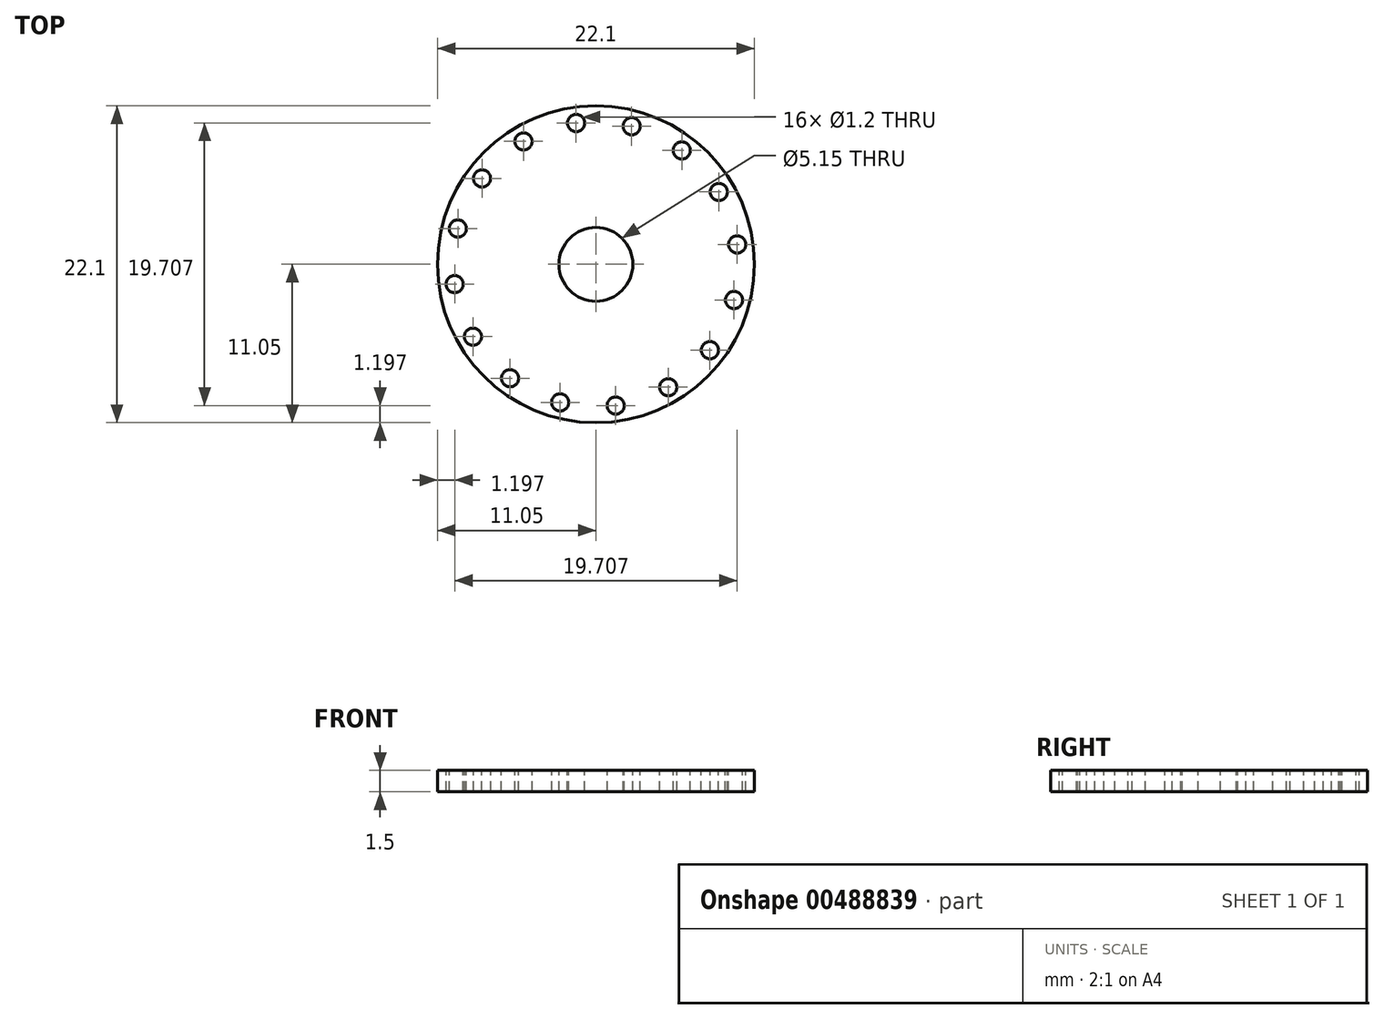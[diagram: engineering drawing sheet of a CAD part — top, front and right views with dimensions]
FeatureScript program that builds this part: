
annotation { "Feature Type Name" : "Feature", "Feature Type Description" : "" }
export const myFeature = defineFeature(function(context is Context, id is Id, definition is map)
    precondition{}
    {
        {
            var Q0;
            Q0=qCreatedBy(makeId("Top.planeOp"),FACE);
            var sketch = newSketch(context, id + "F0", { "sketchPlane" : qUnion([Q0])});
            skCircle(sketch, "E0", {"center": v(0, 0) * mm, "radius": 11.05 * mm});
            skSolve(sketch);
        }
        {
            var Q0;
            Q0=makeQuery(id+"F0.imprint","IMPRINT",FACE,{"disambiguationData":[TD([[makeQuery(id+"F0.imprint","IMPRINT",EDGE,{"derivedFrom":sQuery(id+"F0.wireOp",EDGE,"E0")}),1.0]])]});
            extrude(context, id + "F1", {"entities" : qUnion([Q0]), "depth" : 1.5 * mm, "offsetDistance" : 25 * mm});
        }
        {
            var Q0;
            Q0=makeQuery(id+"F1.opExtrude","CAP_FACE",FACE,{"disambiguationData":[OSD([sQuery(id+"F0.wireOp",EDGE,"E0")])],"isStart":false});
            var sketch = newSketch(context, id + "F2", { "sketchPlane" : qUnion([Q0])});
            skCircle(sketch, "E1", {"center": v(5.99, 7.95) * mm, "radius": 0.6 * mm});
            skPoint(sketch, "E2.center", {"position": v(0, 0) * mm});
            skCircle(sketch, "E3", {"center": v(0, 0) * mm, "radius": 2.58 * mm});
            skLineSegment(sketch, "E4", {"start": v(-5.78, -7.67) * mm, "end": v(0, 0) * mm, "construction": true});
            skCircle(sketch, "E5.1.0", {"center": v(2.5, 9.63) * mm, "radius": 0.6 * mm});
            skCircle(sketch, "E5.2.0", {"center": v(-1.38, 9.85) * mm, "radius": 0.6 * mm});
            skCircle(sketch, "E5.3.0", {"center": v(-5.05, 8.57) * mm, "radius": 0.6 * mm});
            skCircle(sketch, "E5.4.0", {"center": v(-7.95, 5.99) * mm, "radius": 0.6 * mm});
            skCircle(sketch, "E6.1.5.0", {"center": v(-9.63, 2.5) * mm, "radius": 0.6 * mm});
            skCircle(sketch, "E6.1.6.0", {"center": v(-9.85, -1.38) * mm, "radius": 0.6 * mm});
            skCircle(sketch, "E7.1.7.0", {"center": v(-8.57, -5.05) * mm, "radius": 0.6 * mm});
            skCircle(sketch, "E8.1.8.0", {"center": v(-5.99, -7.95) * mm, "radius": 0.6 * mm});
            skCircle(sketch, "E8.1.9.0", {"center": v(-2.5, -9.63) * mm, "radius": 0.6 * mm});
            skCircle(sketch, "E9.1.10.0", {"center": v(1.38, -9.85) * mm, "radius": 0.6 * mm});
            skCircle(sketch, "E9.1.11.0", {"center": v(5.05, -8.57) * mm, "radius": 0.6 * mm});
            skCircle(sketch, "E10.1.12.0", {"center": v(7.95, -5.99) * mm, "radius": 0.6 * mm});
            skCircle(sketch, "E10.1.13.0", {"center": v(9.63, -2.5) * mm, "radius": 0.6 * mm});
            skCircle(sketch, "E10.1.14.0", {"center": v(9.85, 1.38) * mm, "radius": 0.6 * mm});
            skCircle(sketch, "E10.1.15.0", {"center": v(8.57, 5.05) * mm, "radius": 0.6 * mm});
            skSolve(sketch);
        }
        {
            var Q0;
            Q0=makeQuery(id+"F2.imprint","IMPRINT",FACE,{"disambiguationData":[TD([[makeQuery(id+"F2.imprint","IMPRINT",EDGE,{"derivedFrom":sQuery(id+"F2.wireOp",EDGE,"E1")}),1.0]])]});
            var Q1;
            Q1=makeQuery(id+"F2.imprint","IMPRINT",FACE,{"disambiguationData":[TD([[makeQuery(id+"F2.imprint","IMPRINT",EDGE,{"derivedFrom":sQuery(id+"F2.wireOp",EDGE,"E5.4.0")}),1.0]])]});
            var Q2;
            Q2=makeQuery(id+"F2.imprint","IMPRINT",FACE,{"disambiguationData":[TD([[makeQuery(id+"F2.imprint","IMPRINT",EDGE,{"derivedFrom":sQuery(id+"F2.wireOp",EDGE,"E5.3.0")}),1.0]])]});
            var Q3;
            Q3=makeQuery(id+"F2.imprint","IMPRINT",FACE,{"disambiguationData":[TD([[makeQuery(id+"F2.imprint","IMPRINT",EDGE,{"derivedFrom":sQuery(id+"F2.wireOp",EDGE,"E5.2.0")}),1.0]])]});
            var Q4;
            Q4=makeQuery(id+"F2.imprint","IMPRINT",FACE,{"disambiguationData":[TD([[makeQuery(id+"F2.imprint","IMPRINT",EDGE,{"derivedFrom":sQuery(id+"F2.wireOp",EDGE,"E5.1.0")}),1.0]])]});
            var Q5;
            Q5=makeQuery(id+"F2.imprint","IMPRINT",FACE,{"disambiguationData":[TD([[makeQuery(id+"F2.imprint","IMPRINT",EDGE,{"derivedFrom":sQuery(id+"F2.wireOp",EDGE,"E6.1.5.0")}),1.0]])]});
            var Q6;
            Q6=makeQuery(id+"F2.imprint","IMPRINT",FACE,{"disambiguationData":[TD([[makeQuery(id+"F2.imprint","IMPRINT",EDGE,{"derivedFrom":sQuery(id+"F2.wireOp",EDGE,"E6.1.6.0")}),1.0]])]});
            var Q7;
            Q7=makeQuery(id+"F2.imprint","IMPRINT",FACE,{"disambiguationData":[TD([[makeQuery(id+"F2.imprint","IMPRINT",EDGE,{"derivedFrom":sQuery(id+"F2.wireOp",EDGE,"E3")}),1.0]])]});
            var Q8;
            Q8=makeQuery(id+"F2.imprint","IMPRINT",FACE,{"disambiguationData":[TD([[makeQuery(id+"F2.imprint","IMPRINT",EDGE,{"derivedFrom":sQuery(id+"F2.wireOp",EDGE,"E7.1.7.0")}),1.0]])]});
            var Q9;
            Q9=makeQuery(id+"F2.imprint","IMPRINT",FACE,{"disambiguationData":[TD([[makeQuery(id+"F2.imprint","IMPRINT",EDGE,{"derivedFrom":sQuery(id+"F2.wireOp",EDGE,"E8.1.8.0")}),1.0]])]});
            var Q10;
            Q10=makeQuery(id+"F2.imprint","IMPRINT",FACE,{"disambiguationData":[TD([[makeQuery(id+"F2.imprint","IMPRINT",EDGE,{"derivedFrom":sQuery(id+"F2.wireOp",EDGE,"E8.1.9.0")}),1.0]])]});
            var Q11;
            Q11=makeQuery(id+"F2.imprint","IMPRINT",FACE,{"disambiguationData":[TD([[makeQuery(id+"F2.imprint","IMPRINT",EDGE,{"derivedFrom":sQuery(id+"F2.wireOp",EDGE,"E9.1.10.0")}),1.0]])]});
            var Q12;
            Q12=makeQuery(id+"F2.imprint","IMPRINT",FACE,{"disambiguationData":[TD([[makeQuery(id+"F2.imprint","IMPRINT",EDGE,{"derivedFrom":sQuery(id+"F2.wireOp",EDGE,"E9.1.11.0")}),1.0]])]});
            var Q13;
            Q13=makeQuery(id+"F2.imprint","IMPRINT",FACE,{"disambiguationData":[TD([[makeQuery(id+"F2.imprint","IMPRINT",EDGE,{"derivedFrom":sQuery(id+"F2.wireOp",EDGE,"E10.1.12.0")}),1.0]])]});
            var Q14;
            Q14=makeQuery(id+"F2.imprint","IMPRINT",FACE,{"disambiguationData":[TD([[makeQuery(id+"F2.imprint","IMPRINT",EDGE,{"derivedFrom":sQuery(id+"F2.wireOp",EDGE,"E10.1.13.0")}),1.0]])]});
            var Q15;
            Q15=makeQuery(id+"F2.imprint","IMPRINT",FACE,{"disambiguationData":[TD([[makeQuery(id+"F2.imprint","IMPRINT",EDGE,{"derivedFrom":sQuery(id+"F2.wireOp",EDGE,"E10.1.14.0")}),1.0]])]});
            var Q16;
            Q16=makeQuery(id+"F2.imprint","IMPRINT",FACE,{"disambiguationData":[TD([[makeQuery(id+"F2.imprint","IMPRINT",EDGE,{"derivedFrom":sQuery(id+"F2.wireOp",EDGE,"E10.1.15.0")}),1.0]])]});
            extrude(context, id + "F3", {"entities" : qUnion([Q0, Q1, Q2, Q3, Q4, Q5, Q6, Q7, Q8, Q9, Q10, Q11, Q12, Q13, Q14, Q15, Q16]), "operationType" : NewBodyOperationType.REMOVE, "oppositeDirection" : true, "depth" : 25 * mm, "offsetDistance" : 25 * mm});
        }
    });
